# Revit family: PRD_FrankeWS_SlbUrnls_CampusFloorStandingUrinal_BS550
name_source: partatom
category: Plumbing Fixtures
revit_build: Autodesk Revit 2018 (Build: 20190510_1515(x64)
units: mm (PartAtom-declared; Revit-internal decimal feet)

## family parameters
Cut with Voids When Loaded = No
Host = Face
OmniClass Number = 23.45.05.21.11.21
OmniClass Title = Urinals
Part Type = Normal
Room Calculation Point = No
Round Connector Dimension = Use Diameter
Shared = No

## types (1)
- BS550
    AssetType = Fixed
    BIMObjectName = PRD_AR_SlabUrinals_CampusFloorStandingUrinal_BS550
    Category = Pr_40_20_93_77, Slab urinals
    Default Elevation = 0 mm  [stored 0 ft]
    Description = Floor standing urinal, stainless steel, surface satin finished, material thickness 1.5 mm, back inlet button spreaders 1/2 inch. at 600 mm spacings, 1 1/2 inch. flat perforated waste. width: 600 mm
    DiameterNominal = 15  [stored 0.0492126 ft]
    DurationUnit = year
    Features = stainless steel, 1.50 mm, satin finished, wall and floor mounting, 600x1076x260 mm (WxHxD)
    Finish = Satin finished
    Flow = 0.0 L/s
    Form = Floor standing
    GrossWeight = 22.00 kg
    IfcExportAs = IfcSanitaryTerminalType
    IfcExportType = URINAL
    InletSize = DN 15 (1/2 inch.)
    Manufacturer = KWC Group AG
    ManufacturerName = KWC Group AG
    ManufacturerURL = www.kwc.com
    Material = PRD_AR_StainlessSteel_SatinFinished
    MaterialsBody = Stainless steel 1.4301
    MaterialsFinishAndColour = Stainless steel, satin finished
    Model = BS550
    ModelNumber = 2000100030
    ModelReference = BS550
    NBSDescription = Slab urinals
    NBSReference = 45-35-70/352
    Name = CAMPUS floor standing urinal BS550
    NetWeight = 18.00 kg
    NominalDepth = 260 mm  [stored 0.853018 ft]
    NominalLength = 1076 mm  [stored 3.53018 ft]
    NominalWidth = 600 mm  [stored 1.9685 ft]
    OutletSize = DN 40 (1 1/2 inch.)
    ProductInformation = https://pim.kwc.com
    Shape = Rectangular
    Size = 600 x 260 x 1076 mm
    SpilloverLevel = 0 mm  [stored 0 ft]
    URL = www.kwc.com
    Uniclass2015Code = Pr_40_20_93_77
    Uniclass2015Title = Slab urinals
    Uniclass2015Version = Products v1.5
    UrinalColor = Stainless steel
    UrinalMaterial = Stainless steel
    UrinalType = Slab
    Version = 1
    WarrantyDurationUnit = year
    WasteSize = 40  [stored 0.131234 ft]
    WaterSupplyOverflowAndWasteHolesWaste = Center
    WaterSupplyOverflowAndWasteHolesWaterSupply = Back

note: [stored X ft] marks values corroborated as IEEE doubles in the binary element streams (Revit-internal decimal feet)

## geometry (parser evidence)
native form markers: Sweep x4
no freeform markers — native parametric forms only
